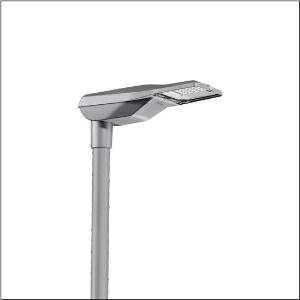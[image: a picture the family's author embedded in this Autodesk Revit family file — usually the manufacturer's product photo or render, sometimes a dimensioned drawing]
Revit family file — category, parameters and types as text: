
# Revit family: streetlight_sl_21_iq_micro___stw1_0a_5xe1e61g08cb_7f5e
name_source: partatom
category: Lighting Fixtures
units: mm (PartAtom-declared; Revit-internal decimal feet)

## family parameters
Cut with Voids When Loaded = No
Host = Face
Light Source = No
Part Type = Normal
Room Calculation Point = No
Round Connector Dimension = Use Diameter
Shared = No

## types (1)
- --- (1 x LED, 2570 lm, 19.4 W, 2700K)
    Apparent Load = 19 VA
    CIE Flux Codes = 38 75 98 100 100
    Color Rendering = 70
    Color Temperature = 2700K
    Default Elevation = 1800 mm
    Description = Streetlight SL 21 iQ micro, mast luminaire, primary light control with lens, of PMMA, primary optical cover: cover, of toughened safety glass, transparent, light distribution: STW1.0a, light emission: direct distribution, primary light characteristic: asymmetric, installation type: post-top, side-entry, LED, High Power LED, rated luminous flux: 2.570lm, luminous efficacy: 133lm/W, light colour: 727, colour temperature: 2700K, control: Street-Remote, Auto-Match, Temp-Guard, Lumen-Switch, Night-Set, Smart-Wire, Light-Fading, Desk-Remote (wireless, voltage-free reading and setting of iQ features in the workshop via application-optimized NFC function/RFID function), optimised constant luminous flux control (CLO 2.0), presetting dimming linear, mains connection: 220..240V, AC, 50/60Hz, start of lifetime: 19W, end of service life: 20W, reduction: 10W, luminaire housing, of diecast aluminium, powder-coated, Siteco® metallic grey (DB 702S), corrosivity category C5 mid according to DIN EN ISO 12944, please order mast flange separately, inclination adjustable: 0°, 5°, 10°, 15°, sealing non-destructively replaceable, multi-level sealing system, length: 528mm, width: 235mm, height: 110mm, mast flange for spigot size: 42mm (side-entry): 5XC10008XM4, 60/48mm (side-entry/post-top): 5XC10108XM2, 76/60mm (side-entry/post-top): 5XC10108XM1, protection rating (complete): IP66, insulation class (complete): insulation class II (safety insulation), certification: CE, ENEC, ENEC+, VDE, impact resistance: IK09, permissible operating ambient temperature for outdoor applications: -40..+50°C, standard-compliant lighting for roads and squares, packaging unit: 1 piece

Light Distribution: STW1.0a
    Height = 110 mm
    Lamp = 1 x LED
    Lamp Light Flux = 2570 lm
    Lamp Power = 19.4 W
    Lamp count = 1
    Length = 528 mm
    Luminous efficacy = 132 lm/W
    Manufacturer = Siteco
    ModVariant = No
    Model = 5XE1E61G08CB
    Number of Poles = 1
    OnlyDefault = Yes
    Power Factor = 1
    Product Name = Streetlight SL 21 iQ micro | STW1.0a
    Product group = mast luminaire | pylon top
    ProductGroupID = 6100
    Protection Class = Protection class II
    Protection Degree = IP 66
    RLX_Detail_Level = 1
    RLX_Emergency_Light_Flux = 0 lm
    RLX_Emergency_Type = 0
    RLX_Emergency_Type_DB = No
    RlxData = <blob elided: 99141 chars, md5=0bf64c02>
    Socket = socket
    Standby Power = 0 W
    System Light Flux = 2570 lm
    System Power = 19 W
    Type Comments = factory setting: luminous flux: 100 % | dim-lin: 254 | 387 mA
    Type Image = l_1006881.jpg
    URL = http://relux.com
    VarID = @adj_070041
    Voltage = 0 V
    Weight = 0.00 kg
    Width = 235 mm

## geometry (parser evidence)
native form markers: Blend x4, Sweep x8
no freeform markers — native parametric forms only
